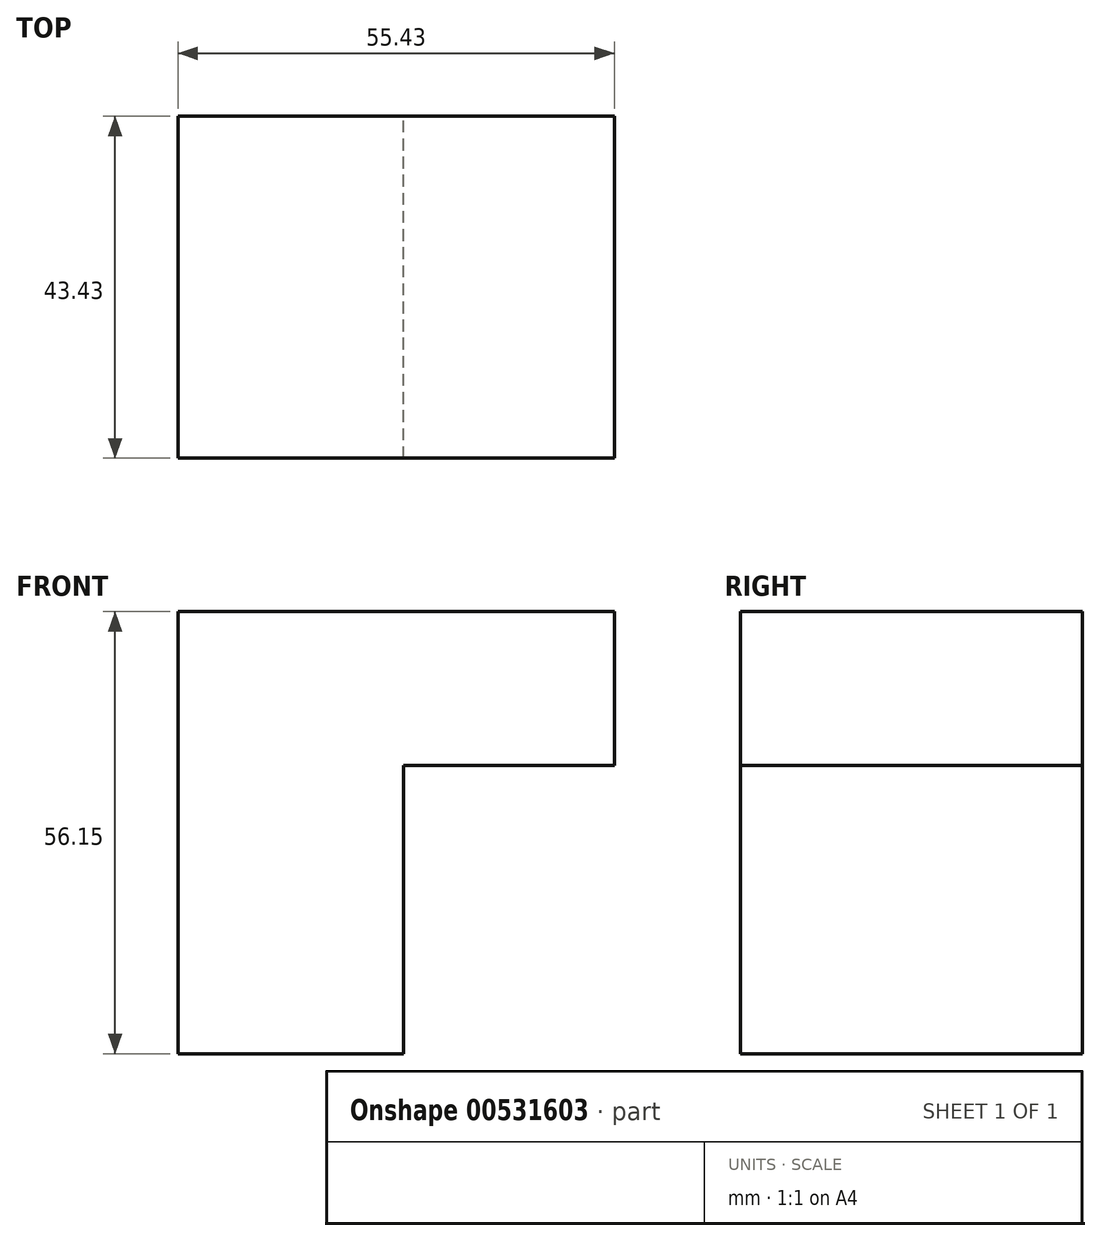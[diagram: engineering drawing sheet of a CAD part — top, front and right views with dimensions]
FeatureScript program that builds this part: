
annotation { "Feature Type Name" : "Feature", "Feature Type Description" : "" }
export const myFeature = defineFeature(function(context is Context, id is Id, definition is map)
    precondition{}
    {
        {
            var Q0;
            Q0=qCreatedBy(makeId("Front.planeOp"),FACE);
            var sketch = newSketch(context, id + "F0", { "sketchPlane" : qUnion([Q0])});
            skLineSegment(sketch, "E0.bottom", {"start": v(0, 0) * mm, "end": v(-55.43, 0) * mm});
            skLineSegment(sketch, "E0.top", {"start": v(0, 56.15) * mm, "end": v(-55.43, 56.15) * mm});
            skLineSegment(sketch, "E0.left", {"start": v(0, 0) * mm, "end": v(0, 56.15) * mm});
            skLineSegment(sketch, "E0.right", {"start": v(-55.43, 0) * mm, "end": v(-55.43, 56.15) * mm});
            skLineSegment(sketch, "E1.bottom", {"start": v(-26.75, -7.71) * mm, "end": v(25.06, -7.71) * mm});
            skLineSegment(sketch, "E1.top", {"start": v(-26.75, 36.63) * mm, "end": v(25.06, 36.63) * mm});
            skLineSegment(sketch, "E1.left", {"start": v(-26.75, -7.71) * mm, "end": v(-26.75, 36.63) * mm});
            skLineSegment(sketch, "E1.right", {"start": v(25.06, -7.71) * mm, "end": v(25.06, 36.63) * mm});
            skSolve(sketch);
        }
        {
            var Q0;
            {var subQ2=sQuery(id+"F0.wireOp",EDGE,"E0.top");Q0=makeQuery(id+"F0.imprint","IMPRINT",FACE,{"disambiguationData":[TD([[makeQuery(id+"F0.imprint","IMPRINT",EDGE,{"derivedFrom":subQ2}),1.0]])]});}
            extrude(context, id + "F1", {"entities" : qUnion([Q0]), "depth" : 43.43 * mm, "offsetDistance" : 25.4 * mm});
        }
    });
